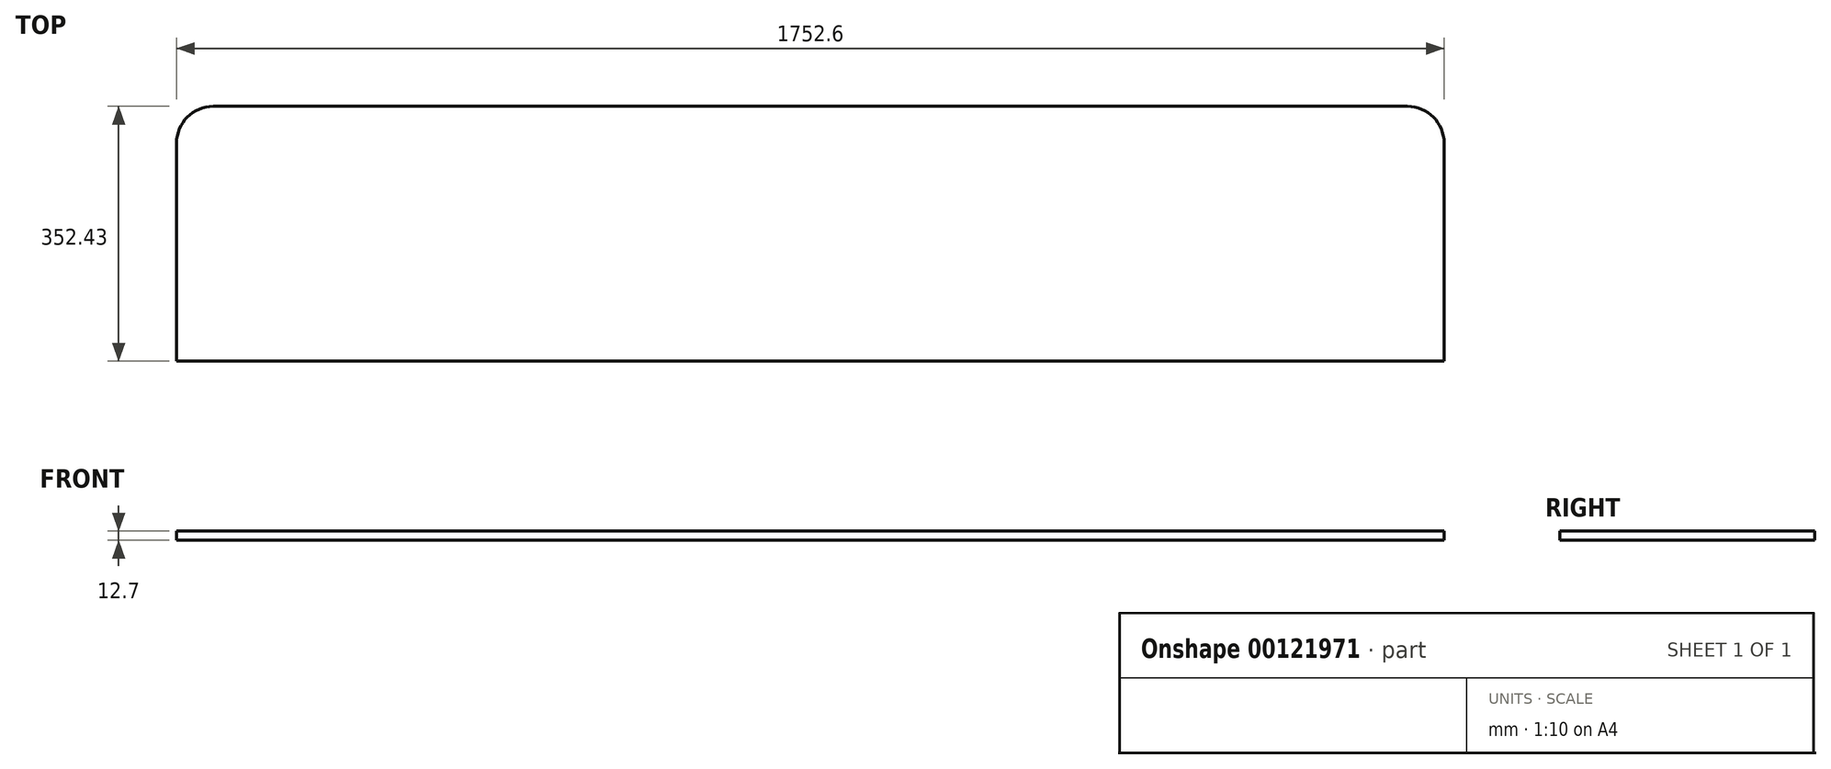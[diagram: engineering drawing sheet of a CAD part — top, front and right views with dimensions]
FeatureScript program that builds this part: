
annotation { "Feature Type Name" : "Feature", "Feature Type Description" : "" }
export const myFeature = defineFeature(function(context is Context, id is Id, definition is map)
    precondition{}
    {
        {
            var Q0;
            Q0=qCreatedBy(makeId("Top.planeOp"),FACE);
            var sketch = newSketch(context, id + "F0", { "sketchPlane" : qUnion([Q0])});
            skLineSegment(sketch, "E0.bottom", {"start": v(0, 0) * mm, "end": v(1752.6, 0) * mm});
            skLineSegment(sketch, "E0.top", {"start": v(50.8, 352.43) * mm, "end": v(1701.8, 352.43) * mm});
            skLineSegment(sketch, "E0.left", {"start": v(0, 0) * mm, "end": v(0, 301.63) * mm});
            skLineSegment(sketch, "E0.right", {"start": v(1752.6, 0) * mm, "end": v(1752.6, 301.63) * mm});
            skPoint(sketch, "E1.visualSharp", {"position": v(0, 352.43) * mm});
            skArc(sketch, "E1.filletArc", {"start": v(50.8, 352.43) * mm, "mid": v(14.88, 337.55) * mm, "end": v(0, 301.63) * mm});
            skPoint(sketch, "E2.visualSharp", {"position": v(1752.6, 352.43) * mm});
            skArc(sketch, "E2.filletArc", {"start": v(1752.6, 301.63) * mm, "mid": v(1737.72, 337.55) * mm, "end": v(1701.8, 352.43) * mm});
            skSolve(sketch);
        }
        {
            var Q0;
            Q0 = qSketchRegion(id + "F0", true);
            extrude(context, id + "F1", {"entities" : qUnion([Q0]), "depth" : 12.7 * mm});
        }
    });
